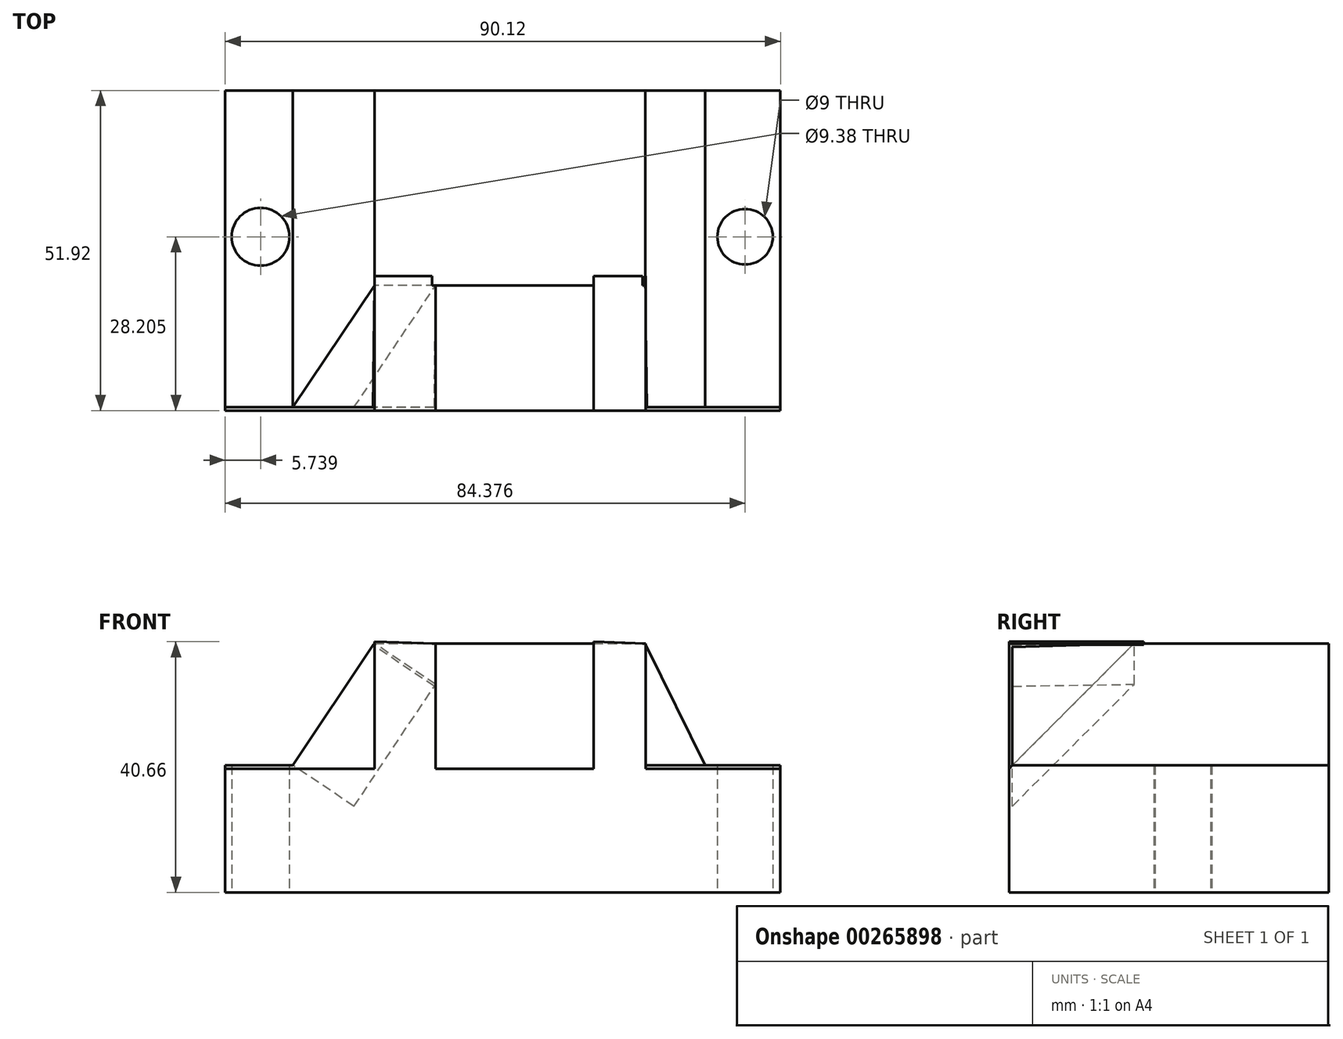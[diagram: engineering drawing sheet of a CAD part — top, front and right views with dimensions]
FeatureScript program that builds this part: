
annotation { "Feature Type Name" : "Feature", "Feature Type Description" : "" }
export const myFeature = defineFeature(function(context is Context, id is Id, definition is map)
    precondition{}
    {
        {
            var Q0;
            Q0=qCreatedBy(makeId("Top.planeOp"),FACE);
            var sketch = newSketch(context, id + "F0", { "sketchPlane" : qUnion([Q0])});
            skLineSegment(sketch, "E0.bottom", {"start": v(-46.68, 30.83) * mm, "end": v(43.44, 30.83) * mm});
            skLineSegment(sketch, "E0.top", {"start": v(-46.68, -21.1) * mm, "end": v(43.44, -21.1) * mm});
            skLineSegment(sketch, "E0.left", {"start": v(-46.68, 30.83) * mm, "end": v(-46.68, -21.1) * mm});
            skLineSegment(sketch, "E0.right", {"start": v(43.44, 30.83) * mm, "end": v(43.44, -21.1) * mm});
            skSolve(sketch);
        }
        {
            var Q0;
            Q0 = qSketchRegion(id + "F0", true);
            extrude(context, id + "F1", {"entities" : qUnion([Q0]), "depth" : 40.4 * mm});
        }
        {
            var Q0;
            Q0=makeQuery(id+"F1.opExtrude","SWEPT_FACE",FACE,{"disambiguationData":[OSD([sQuery(id+"F0.wireOp",EDGE,"E0.top")])]});
            var sketch = newSketch(context, id + "F2", { "sketchPlane" : qUnion([Q0])});
            skLineSegment(sketch, "E1", {"start": v(21.47, 40.39) * mm, "end": v(31.2, 20.6) * mm});
            skLineSegment(sketch, "E2", {"start": v(31.2, 20.6) * mm, "end": v(43.44, 20.6) * mm});
            skLineSegment(sketch, "E3", {"start": v(43.44, 20.6) * mm, "end": v(43.44, 40.39) * mm});
            skLineSegment(sketch, "E4", {"start": v(43.44, 40.39) * mm, "end": v(21.47, 40.39) * mm});
            skLineSegment(sketch, "E5", {"start": v(-46.68, 20.6) * mm, "end": v(-32.95, 20.6) * mm});
            skPoint(sketch, "E5.endSnap0", {"position": v(37.32, 20.6) * mm});
            skLineSegment(sketch, "E6", {"start": v(-32.95, 20.6) * mm, "end": v(-46.68, 20.6) * mm});
            skLineSegment(sketch, "E7", {"start": v(43.44, 20.6) * mm, "end": v(31.2, 20.6) * mm});
            skLineSegment(sketch, "E8", {"start": v(-46.68, 20.6) * mm, "end": v(-35.7, 20.6) * mm});
            skLineSegment(sketch, "E9", {"start": v(-35.7, 20.6) * mm, "end": v(-22.47, 40.39) * mm});
            skLineSegment(sketch, "E10", {"start": v(-22.47, 40.39) * mm, "end": v(-46.68, 40.39) * mm});
            skLineSegment(sketch, "E11", {"start": v(-46.68, 40.39) * mm, "end": v(-46.68, 20.6) * mm});
            skSolve(sketch);
        }
        {
            var Q0;
            Q0 = qSketchRegion(id + "F2", true);
            extrude(context, id + "F3", {"entities" : qUnion([Q0]), "operationType" : NewBodyOperationType.REMOVE, "oppositeDirection" : true, "depth" : 91.95 * mm});
        }
        {
            var Q0;
            Q0=qCreatedBy(makeId("Top.planeOp"),FACE);
            var sketch = newSketch(context, id + "F4", { "sketchPlane" : qUnion([Q0])});
            skCircle(sketch, "E12", {"center": v(37.7, 7.11) * mm, "radius": 4.5 * mm});
            skCircle(sketch, "E13", {"center": v(-40.94, 7.11) * mm, "radius": 4.7 * mm});
            skSolve(sketch);
        }
        {
            var Q0;
            Q0 = qSketchRegion(id + "F4", true);
            extrude(context, id + "F5", {"entities" : qUnion([Q0]), "operationType" : NewBodyOperationType.REMOVE, "depth" : 57.4 * mm});
        }
        {
            var Q0;
            Q0=makeQuery(id+"F1.opExtrude","CAP_EDGE",EDGE,{"disambiguationData":[OSD([sQuery(id+"F0.wireOp",EDGE,"E0.top")])],"isStart":false});
            chamfer(context, id + "F6", {"entities" : qUnion([Q0]), "width" : 20.32 * mm, "tangentPropagation" : true});
        }
        {
            var Q0;
            Q0=makeQuery(id+"F1.opExtrude","SWEPT_FACE",FACE,{"disambiguationData":[OSD([sQuery(id+"F0.wireOp",EDGE,"E0.top")])]});
            var sketch = newSketch(context, id + "F7", { "sketchPlane" : qUnion([Q0])});
            skLineSegment(sketch, "E14", {"start": v(-22.44, 40.66) * mm, "end": v(-22.44, 0) * mm});
            skLineSegment(sketch, "E15", {"start": v(-22.44, 0) * mm, "end": v(-12.53, 0) * mm});
            skLineSegment(sketch, "E16", {"start": v(-12.53, 0) * mm, "end": v(-12.53, 40.37) * mm});
            skLineSegment(sketch, "E17", {"start": v(-12.53, 40.37) * mm, "end": v(-22.44, 40.66) * mm});
            skLineSegment(sketch, "E18", {"start": v(21.57, 40.37) * mm, "end": v(21.57, 0) * mm});
            skLineSegment(sketch, "E19", {"start": v(21.57, 0) * mm, "end": v(13.12, 0) * mm});
            skLineSegment(sketch, "E20", {"start": v(13.12, 0) * mm, "end": v(13.12, 40.66) * mm});
            skLineSegment(sketch, "E21", {"start": v(13.12, 40.66) * mm, "end": v(21.57, 40.37) * mm});
            skSolve(sketch);
        }
        {
            var Q0;
            Q0 = qSketchRegion(id + "F7", true);
            extrude(context, id + "F8", {"entities" : qUnion([Q0]), "operationType" : NewBodyOperationType.ADD, "oppositeDirection" : true, "depth" : 21.84 * mm});
        }
        {
            var Q0;
            Q0=makeQuery(id+"F3.boolean.opBoolean","COPY",FACE,{"derivedFrom":makeQuery(id+"F3.opExtrude","SWEPT_FACE",FACE,{"disambiguationData":[OSD([sQuery(id+"F2.wireOp",EDGE,"E9")])]})});
            var sketch = newSketch(context, id + "F9", { "sketchPlane" : qUnion([Q0])});
            skLineSegment(sketch, "E22", {"start": v(20.57, -2.72) * mm, "end": v(20.57, 20.72) * mm});
            skLineSegment(sketch, "E23", {"start": v(20.57, 20.72) * mm, "end": v(0.77, 21.09) * mm});
            skLineSegment(sketch, "E24", {"start": v(0.77, 21.09) * mm, "end": v(20.57, -2.72) * mm});
            skSolve(sketch);
        }
        {
            var Q0;
            Q0 = qSketchRegion(id + "F9", true);
            extrude(context, id + "F10", {"entities" : qUnion([Q0]), "oppositeDirection" : true, "depth" : 11.94 * mm});
        }
        {
            var Q0;
            Q0=makeQuery(id+"F3.boolean.opBoolean","COPY",FACE,{"derivedFrom":makeQuery(id+"F3.opExtrude","SWEPT_FACE",FACE,{"disambiguationData":[OSD([sQuery(id+"F2.wireOp",EDGE,"E1")])]})});
            var sketch = newSketch(context, id + "F11", { "sketchPlane" : qUnion([Q0])});
            skLineSegment(sketch, "E25", {"start": v(-20.57, 4.7) * mm, "end": v(-20.57, 26.1) * mm});
            skLineSegment(sketch, "E26", {"start": v(-20.57, 26.1) * mm, "end": v(-0.77, 26.76) * mm});
            skLineSegment(sketch, "E27", {"start": v(-0.77, 26.76) * mm, "end": v(-20.57, 4.7) * mm});
            skSolve(sketch);
        }
        {
            var Q0;
            Q0 = qSketchRegion(id + "F11", true);
            extrude(context, id + "F12", {"entities" : qUnion([Q0]), "operationType" : NewBodyOperationType.ADD, "oppositeDirection" : true, "depth" : 8.9 * mm});
        }
    });
